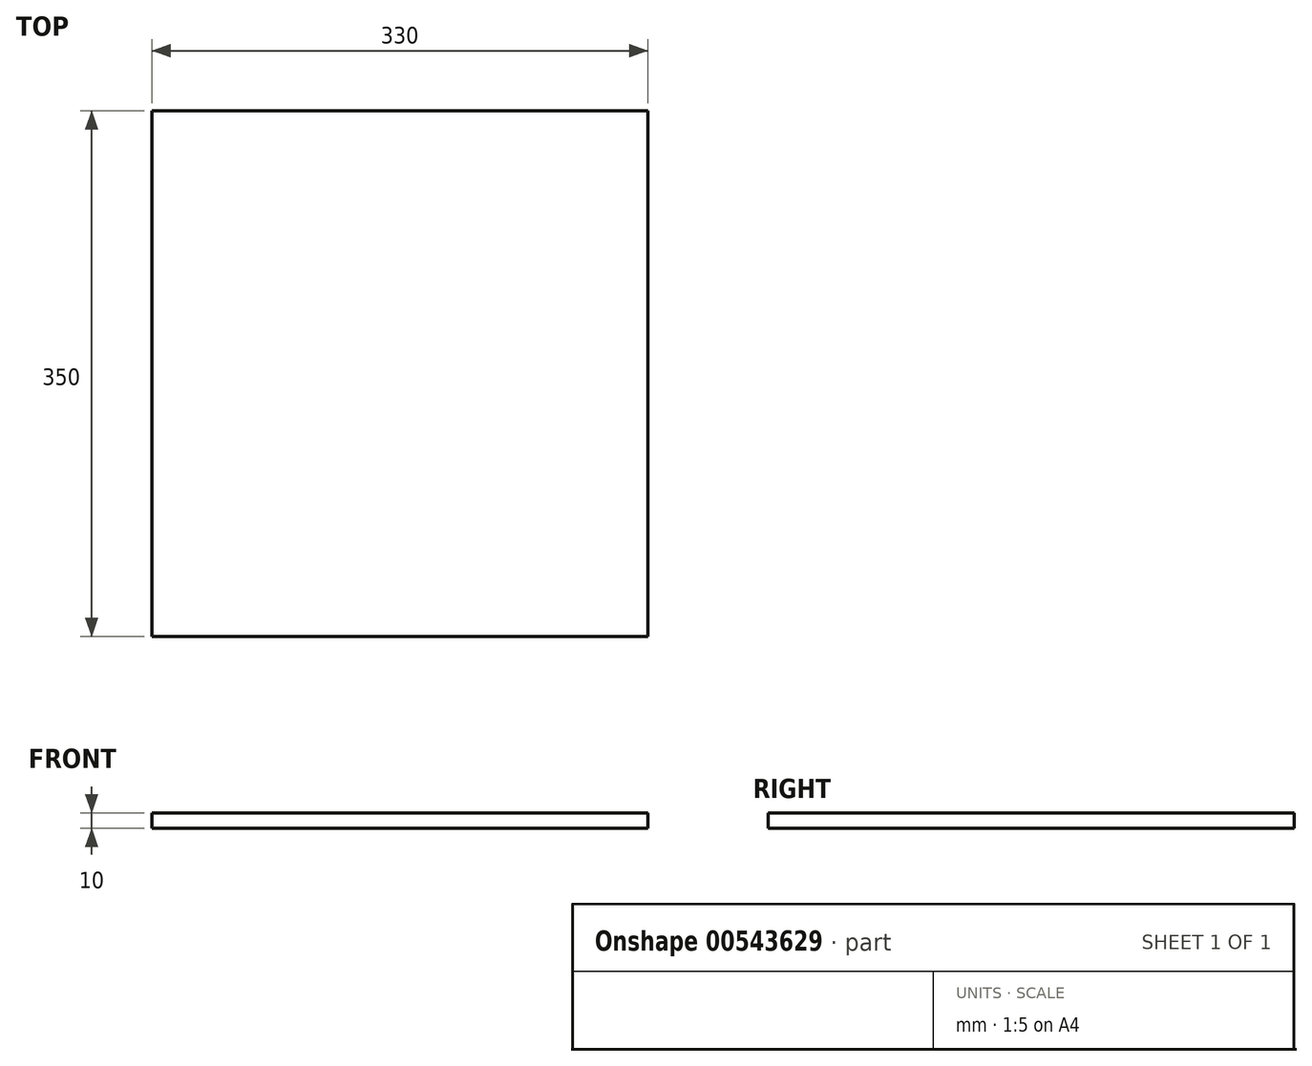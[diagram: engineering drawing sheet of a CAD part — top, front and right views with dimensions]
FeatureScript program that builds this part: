
annotation { "Feature Type Name" : "Feature", "Feature Type Description" : "" }
export const myFeature = defineFeature(function(context is Context, id is Id, definition is map)
    precondition{}
    {
        {
            var Q0;
            Q0=qCreatedBy(makeId("Top.planeOp"),FACE);
            var sketch = newSketch(context, id + "F0", { "sketchPlane" : qUnion([Q0])});
            skLineSegment(sketch, "E0.bottom", {"start": v(-70.96, 65.05) * mm, "end": v(259.04, 65.05) * mm});
            skLineSegment(sketch, "E0.top", {"start": v(-70.96, -284.95) * mm, "end": v(259.04, -284.95) * mm});
            skLineSegment(sketch, "E0.left", {"start": v(-70.96, 65.05) * mm, "end": v(-70.96, -284.95) * mm});
            skLineSegment(sketch, "E0.right", {"start": v(259.04, 65.05) * mm, "end": v(259.04, -284.95) * mm});
            skSolve(sketch);
        }
        {
            var Q0;
            Q0=qSketchRegion(id+"F0",true);
            extrude(context, id + "F1", {"entities" : qUnion([Q0]), "depth" : 10 * mm});
        }
    });
